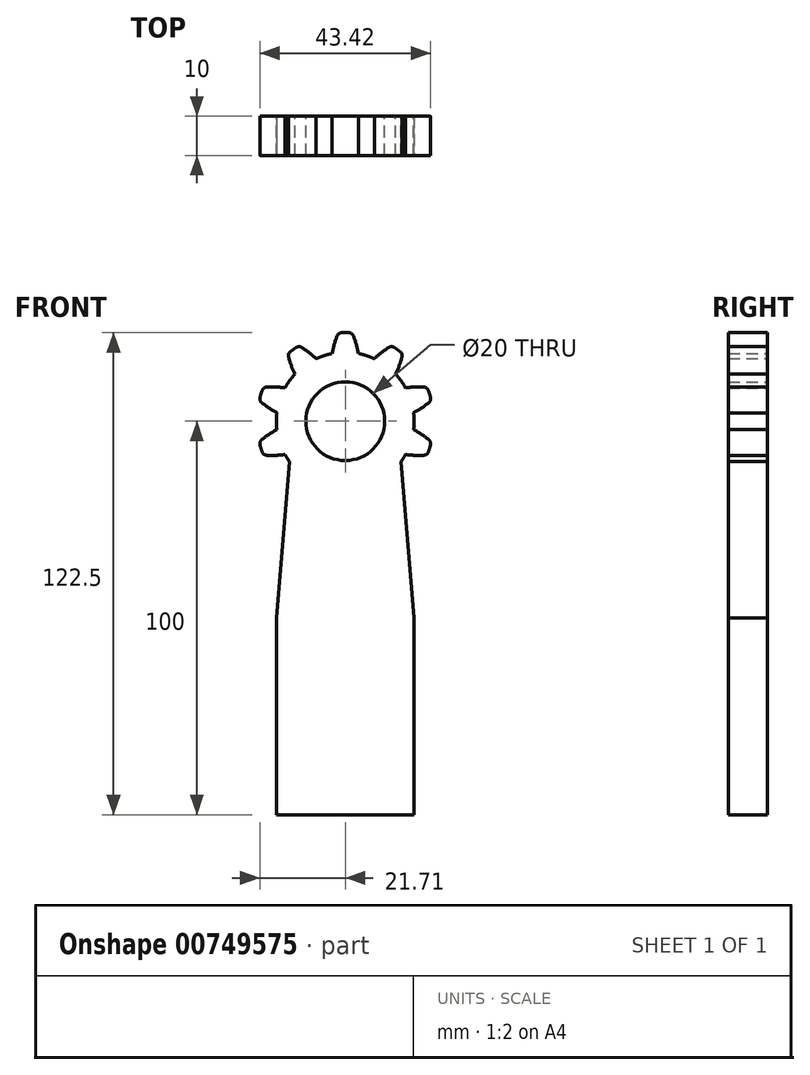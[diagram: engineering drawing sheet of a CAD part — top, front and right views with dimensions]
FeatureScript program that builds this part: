
annotation { "Feature Type Name" : "Feature", "Feature Type Description" : "" }
export const myFeature = defineFeature(function(context is Context, id is Id, definition is map)
    precondition{}
    {
        {
            var Q0;
            Q0=qCreatedBy(makeId("Front.planeOp"),FACE);
            var sketch = newSketch(context, id + "F0", { "sketchPlane" : qUnion([Q0])});
            skLineSegment(sketch, "E0", {"start": v(17.5, -100) * mm, "end": v(-17.5, -100) * mm});
            skLineSegment(sketch, "E1", {"start": v(-17.5, -100) * mm, "end": v(-17.5, -50) * mm});
            skArc(sketch, "E2", {"start": v(14.16, -10.29) * mm, "mid": v(14.76, -9.4) * mm, "end": v(15.3, -8.48) * mm});
            skArc(sketch, "E3", {"start": v(21.1, -7.82) * mm, "mid": v(21.25, -7.39) * mm, "end": v(21.4, -6.95) * mm});
            skArc(sketch, "E4", {"start": v(15.3, -8.48) * mm, "mid": v(17.62, -8.68) * mm, "end": v(19.95, -8.67) * mm});
            skArc(sketch, "E5.MirrorCS", {"start": v(21.67, -6.07) * mm, "mid": v(21.54, -6.51) * mm, "end": v(21.4, -6.95) * mm});
            skArc(sketch, "E6.MirrorCS", {"start": v(17.37, -2.13) * mm, "mid": v(19.36, -3.33) * mm, "end": v(21.23, -4.71) * mm});
            skArc(sketch, "E7.MirrorCS", {"start": v(17.5, 0) * mm, "mid": v(17.47, -1.07) * mm, "end": v(17.37, -2.13) * mm});
            skPoint(sketch, "E8.visualSharp", {"position": v(20.79, -8.61) * mm});
            skArc(sketch, "E8.filletArc", {"start": v(19.95, -8.67) * mm, "mid": v(20.65, -8.42) * mm, "end": v(21.1, -7.82) * mm});
            skPoint(sketch, "E9.visualSharp", {"position": v(21.88, -5.25) * mm});
            skArc(sketch, "E9.filletArc", {"start": v(21.67, -6.07) * mm, "mid": v(21.65, -5.33) * mm, "end": v(21.23, -4.71) * mm});
            skLineSegment(sketch, "E10", {"start": v(14.16, -10.29) * mm, "end": v(17.5, -50) * mm});
            skLineSegment(sketch, "E11.trimOffspring", {"start": v(17.5, -50) * mm, "end": v(17.5, -100) * mm});
            skArc(sketch, "E12.1.0", {"start": v(17.37, 2.13) * mm, "mid": v(19.36, 3.33) * mm, "end": v(21.23, 4.71) * mm});
            skArc(sketch, "E12.1.1", {"start": v(15.3, 8.48) * mm, "mid": v(17.62, 8.68) * mm, "end": v(19.95, 8.67) * mm});
            skArc(sketch, "E12.1.2", {"start": v(17.5, 0) * mm, "mid": v(17.47, 1.07) * mm, "end": v(17.37, 2.13) * mm});
            skPoint(sketch, "E12.1.3", {"position": v(21.88, 5.25) * mm});
            skArc(sketch, "E12.1.4", {"start": v(14.16, 10.29) * mm, "mid": v(14.76, 9.4) * mm, "end": v(15.3, 8.48) * mm});
            skPoint(sketch, "E12.1.5", {"position": v(20.79, 8.61) * mm});
            skArc(sketch, "E12.1.6", {"start": v(21.1, 7.82) * mm, "mid": v(20.65, 8.42) * mm, "end": v(19.95, 8.67) * mm});
            skArc(sketch, "E12.1.7", {"start": v(21.23, 4.71) * mm, "mid": v(21.65, 5.33) * mm, "end": v(21.67, 6.07) * mm});
            skArc(sketch, "E12.1.8", {"start": v(21.1, 7.82) * mm, "mid": v(21.25, 7.39) * mm, "end": v(21.4, 6.95) * mm});
            skArc(sketch, "E12.1.9", {"start": v(21.67, 6.07) * mm, "mid": v(21.54, 6.51) * mm, "end": v(21.4, 6.95) * mm});
            skArc(sketch, "E12.2.0", {"start": v(12.8, 11.93) * mm, "mid": v(13.7, 14.08) * mm, "end": v(14.4, 16.3) * mm});
            skArc(sketch, "E12.2.1", {"start": v(7.4, 15.86) * mm, "mid": v(9.15, 17.38) * mm, "end": v(11.04, 18.74) * mm});
            skArc(sketch, "E12.2.2", {"start": v(14.16, 10.29) * mm, "mid": v(13.5, 11.13) * mm, "end": v(12.8, 11.93) * mm});
            skPoint(sketch, "E12.2.3", {"position": v(14.61, 17.1) * mm});
            skArc(sketch, "E12.2.4", {"start": v(5.4, 16.64) * mm, "mid": v(6.41, 16.28) * mm, "end": v(7.4, 15.86) * mm});
            skPoint(sketch, "E12.2.5", {"position": v(11.76, 19.18) * mm});
            skArc(sketch, "E12.2.6", {"start": v(12.47, 18.73) * mm, "mid": v(11.76, 18.95) * mm, "end": v(11.04, 18.74) * mm});
            skArc(sketch, "E12.2.7", {"start": v(14.4, 16.3) * mm, "mid": v(14.39, 17.04) * mm, "end": v(13.96, 17.65) * mm});
            skArc(sketch, "E12.2.8", {"start": v(12.47, 18.73) * mm, "mid": v(12.85, 18.47) * mm, "end": v(13.23, 18.2) * mm});
            skArc(sketch, "E12.2.9", {"start": v(13.96, 17.65) * mm, "mid": v(13.6, 17.93) * mm, "end": v(13.23, 18.2) * mm});
            skArc(sketch, "E12.3.0", {"start": v(3.34, 17.18) * mm, "mid": v(2.81, 19.44) * mm, "end": v(2.08, 21.65) * mm});
            skArc(sketch, "E12.3.1", {"start": v(-3.34, 17.18) * mm, "mid": v(-2.81, 19.44) * mm, "end": v(-2.08, 21.65) * mm});
            skArc(sketch, "E12.3.2", {"start": v(5.4, 16.64) * mm, "mid": v(4.38, 16.94) * mm, "end": v(3.34, 17.18) * mm});
            skPoint(sketch, "E12.3.3", {"position": v(1.77, 22.43) * mm});
            skArc(sketch, "E12.3.4", {"start": v(-5.4, 16.64) * mm, "mid": v(-4.38, 16.94) * mm, "end": v(-3.34, 17.18) * mm});
            skPoint(sketch, "E12.3.5", {"position": v(-1.77, 22.43) * mm});
            skArc(sketch, "E12.3.6", {"start": v(-0.92, 22.48) * mm, "mid": v(-1.63, 22.24) * mm, "end": v(-2.08, 21.65) * mm});
            skArc(sketch, "E12.3.7", {"start": v(2.08, 21.65) * mm, "mid": v(1.63, 22.24) * mm, "end": v(0.92, 22.48) * mm});
            skArc(sketch, "E12.3.8", {"start": v(-0.92, 22.48) * mm, "mid": v(-0.46, 22.5) * mm, "end": v(0, 22.5) * mm});
            skArc(sketch, "E12.3.9", {"start": v(0.92, 22.48) * mm, "mid": v(0.46, 22.5) * mm, "end": v(0, 22.5) * mm});
            skArc(sketch, "E12.4.0", {"start": v(-7.4, 15.86) * mm, "mid": v(-9.15, 17.38) * mm, "end": v(-11.04, 18.74) * mm});
            skArc(sketch, "E12.4.1", {"start": v(-12.8, 11.94) * mm, "mid": v(-13.7, 14.08) * mm, "end": v(-14.4, 16.3) * mm});
            skArc(sketch, "E12.4.2", {"start": v(-5.4, 16.64) * mm, "mid": v(-6.41, 16.28) * mm, "end": v(-7.4, 15.86) * mm});
            skPoint(sketch, "E12.4.3", {"position": v(-11.76, 19.18) * mm});
            skArc(sketch, "E12.4.4", {"start": v(-14.16, 10.29) * mm, "mid": v(-13.5, 11.13) * mm, "end": v(-12.8, 11.94) * mm});
            skPoint(sketch, "E12.4.5", {"position": v(-14.61, 17.1) * mm});
            skArc(sketch, "E12.4.6", {"start": v(-13.96, 17.65) * mm, "mid": v(-14.39, 17.04) * mm, "end": v(-14.4, 16.3) * mm});
            skArc(sketch, "E12.4.7", {"start": v(-11.04, 18.74) * mm, "mid": v(-11.76, 18.95) * mm, "end": v(-12.47, 18.73) * mm});
            skArc(sketch, "E12.4.8", {"start": v(-13.96, 17.65) * mm, "mid": v(-13.6, 17.93) * mm, "end": v(-13.23, 18.2) * mm});
            skArc(sketch, "E12.4.9", {"start": v(-12.47, 18.73) * mm, "mid": v(-12.85, 18.47) * mm, "end": v(-13.23, 18.2) * mm});
            skArc(sketch, "E12.5.0", {"start": v(-15.3, 8.48) * mm, "mid": v(-17.62, 8.68) * mm, "end": v(-19.95, 8.67) * mm});
            skArc(sketch, "E12.5.1", {"start": v(-17.37, 2.13) * mm, "mid": v(-19.36, 3.33) * mm, "end": v(-21.23, 4.71) * mm});
            skArc(sketch, "E12.5.2", {"start": v(-14.16, 10.29) * mm, "mid": v(-14.76, 9.4) * mm, "end": v(-15.3, 8.48) * mm});
            skPoint(sketch, "E12.5.3", {"position": v(-20.79, 8.61) * mm});
            skArc(sketch, "E12.5.4", {"start": v(-17.5, 0) * mm, "mid": v(-17.47, 1.07) * mm, "end": v(-17.37, 2.13) * mm});
            skPoint(sketch, "E12.5.5", {"position": v(-21.88, 5.25) * mm});
            skArc(sketch, "E12.5.6", {"start": v(-21.67, 6.07) * mm, "mid": v(-21.65, 5.33) * mm, "end": v(-21.23, 4.71) * mm});
            skArc(sketch, "E12.5.7", {"start": v(-19.95, 8.67) * mm, "mid": v(-20.65, 8.42) * mm, "end": v(-21.1, 7.82) * mm});
            skArc(sketch, "E12.5.8", {"start": v(-21.67, 6.07) * mm, "mid": v(-21.54, 6.51) * mm, "end": v(-21.4, 6.95) * mm});
            skArc(sketch, "E12.5.9", {"start": v(-21.1, 7.82) * mm, "mid": v(-21.25, 7.39) * mm, "end": v(-21.4, 6.95) * mm});
            skArc(sketch, "E12.6.0", {"start": v(-17.37, -2.13) * mm, "mid": v(-19.36, -3.33) * mm, "end": v(-21.23, -4.71) * mm});
            skArc(sketch, "E12.6.1", {"start": v(-15.3, -8.48) * mm, "mid": v(-17.62, -8.68) * mm, "end": v(-19.95, -8.67) * mm});
            skArc(sketch, "E12.6.2", {"start": v(-17.5, 0) * mm, "mid": v(-17.47, -1.07) * mm, "end": v(-17.37, -2.13) * mm});
            skPoint(sketch, "E12.6.3", {"position": v(-21.88, -5.25) * mm});
            skArc(sketch, "E12.6.4", {"start": v(-14.16, -10.29) * mm, "mid": v(-14.76, -9.4) * mm, "end": v(-15.3, -8.48) * mm});
            skPoint(sketch, "E12.6.5", {"position": v(-20.79, -8.61) * mm});
            skArc(sketch, "E12.6.6", {"start": v(-21.1, -7.82) * mm, "mid": v(-20.65, -8.42) * mm, "end": v(-19.95, -8.67) * mm});
            skArc(sketch, "E12.6.7", {"start": v(-21.23, -4.71) * mm, "mid": v(-21.65, -5.33) * mm, "end": v(-21.67, -6.07) * mm});
            skArc(sketch, "E12.6.8", {"start": v(-21.1, -7.82) * mm, "mid": v(-21.25, -7.39) * mm, "end": v(-21.4, -6.95) * mm});
            skArc(sketch, "E12.6.9", {"start": v(-21.67, -6.07) * mm, "mid": v(-21.54, -6.51) * mm, "end": v(-21.4, -6.95) * mm});
            skLineSegment(sketch, "E12.6.10", {"start": v(-14.16, -10.29) * mm, "end": v(-14.17, -10.27) * mm});
            skLineSegment(sketch, "E13", {"start": v(-14.16, -10.29) * mm, "end": v(-17.5, -50) * mm});
            skCircle(sketch, "E14", {"center": v(0, 0) * mm, "radius": 10 * mm});
            skPoint(sketch, "E15.start.orphan", {"position": v(17.5, 0) * mm});
            skPoint(sketch, "E16.trimOffspring.end.orphan", {"position": v(-17.5, 0) * mm});
            skSolve(sketch);
        }
        {
            var Q0;
            Q0=makeQuery(id+"F0.imprint","IMPRINT",FACE,{"disambiguationData":[TD([[makeQuery(id+"F0.imprint","IMPRINT",EDGE,{"derivedFrom":sQuery(id+"F0.wireOp",EDGE,"E0")}),-1.0]])]});
            extrude(context, id + "F1", {"entities" : qUnion([Q0]), "depth" : 10 * mm, "offsetDistance" : 25 * mm});
        }
    });
